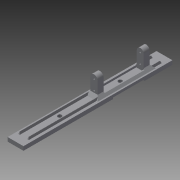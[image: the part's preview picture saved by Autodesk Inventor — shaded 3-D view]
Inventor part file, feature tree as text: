
AUTODESK INVENTOR PART (.ipt)
format: ipt  version: 2015 (Build 190159000, 159)  size: 205,312 bytes
history: native  units: in
note: dims shown in document units (in); Inventor stores cm internally (conversion verified against a paired STEP export)
features: extrude x8, sketch x8, reference x8, projected_geometry x3, chamfer x2, fillet x1
ambient origin geometry x8: Origin, YZ Plane, XZ Plane, XY Plane, X Axis, Y Axis, Z Axis, Center Point
bodies: Solid1 (feature_tree)
feature tree (30):
  extrude  "Extrusion1"  Depth=0.25in
  extrude  "Extrusion2"  Depth=0.25in
  extrude  "Extrusion3"  Depth=0.25in TaperAngle=0.0deg
  extrude  "Extrusion4"  Depth=2.075in TaperAngle=0.0deg
  chamfer  "Chamfer1"  Distance=1.1875in
  extrude  "Extrusion5"  Depth=0.125in TaperAngle=0.0deg
  fillet  "Fillet1"  Radius=0.25in
  chamfer  "Chamfer2"  Distance=0.125in Angle=45.0deg
  extrude  "Extrusion6"  Depth=0.125in TaperAngle=0.0deg
  extrude  "Extrusion7"  Depth=0.125in TaperAngle=0.0deg
  extrude  "Extrusion8"  [1 undecoded]
  sketch  "Sketch1"  dims[d0=1.0in d1=0.25in]
  sketch  "Sketch2"  dims[d2=9.3625in d3=0.0in d6=0.25in]
  projected_geometry  "Projected Loop1"
  sketch  "Sketch3"  dims[d7=0.25in d8=4.8in d9=0.0in]
  sketch  "Sketch4"  dims[d10=3.8in d11=2.075in d12=0.0in]
  reference  "Reference1"
  reference  "Reference2"
  sketch  "Sketch5"  dims[d13=0.375in]
  reference  "Reference3"
  reference  "Reference4"
  sketch  "Sketch6"  dims[d14=0.375in d15=1.1875in d16=0.0in]
  sketch  "Sketch7"  dims[d17=0.1875in d18=0.125in d19=45.0deg d20=1.25in d21=0.0in d22=0.25in d23=0.1875in d24=0.125in d25=45.0deg]
  reference  "Reference5"
  reference  "Reference6"
  reference  "Reference7"
  sketch  "Sketch8"  dims[d26=0.1875in d27=-0.1374in d28=0.125in d29=0.0in d30=0.125in d31=0.0in]
  projected_geometry  "Projected Loop2"
  projected_geometry  "Projected Loop3"
  reference  "Reference10"
note: 1 required parameter value undecoded (feature->parameter linkage not recoverable at this tier; creation-order binding heuristic only, values carry confidence <= 0.55)
